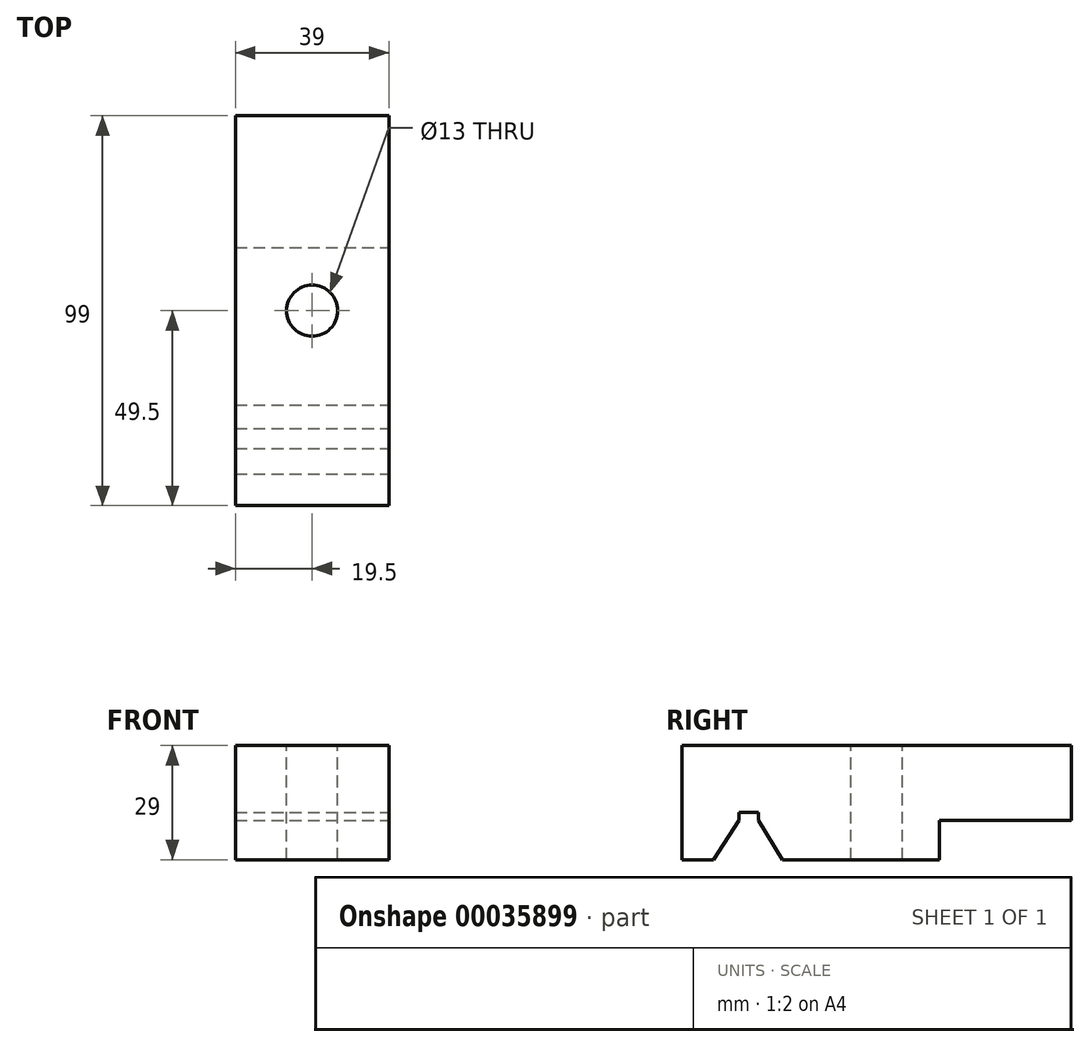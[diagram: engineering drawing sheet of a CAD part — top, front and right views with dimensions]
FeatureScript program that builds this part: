
annotation { "Feature Type Name" : "Feature", "Feature Type Description" : "" }
export const myFeature = defineFeature(function(context is Context, id is Id, definition is map)
    precondition{}
    {
        {
            var Q0;
            Q0=qCreatedBy(makeId("Right.planeOp"),FACE);
            var sketch = newSketch(context, id + "F0", { "sketchPlane" : qUnion([Q0])});
            skLineSegment(sketch, "E0", {"start": v(0, 0) * mm, "end": v(49.5, 0) * mm});
            skLineSegment(sketch, "E1", {"start": v(49.5, 0) * mm, "end": v(49.5, -19) * mm});
            skLineSegment(sketch, "E2", {"start": v(49.5, -19) * mm, "end": v(16, -19) * mm});
            skLineSegment(sketch, "E3", {"start": v(16, -19) * mm, "end": v(16, -29) * mm});
            skLineSegment(sketch, "E4", {"start": v(16, -29) * mm, "end": v(-24, -29) * mm});
            skLineSegment(sketch, "E5", {"start": v(-24, -29) * mm, "end": v(-30, -19) * mm});
            skLineSegment(sketch, "E6", {"start": v(-30, -19) * mm, "end": v(-30, -17) * mm});
            skLineSegment(sketch, "E7", {"start": v(-30, -17) * mm, "end": v(-35, -17) * mm});
            skLineSegment(sketch, "E8", {"start": v(-35, -17) * mm, "end": v(-35, -19) * mm});
            skLineSegment(sketch, "E9", {"start": v(-35, -19) * mm, "end": v(-41.5, -29) * mm});
            skLineSegment(sketch, "E10", {"start": v(-41.5, -29) * mm, "end": v(-49.5, -29) * mm});
            skLineSegment(sketch, "E11", {"start": v(-49.5, -29) * mm, "end": v(-49.5, 0) * mm});
            skLineSegment(sketch, "E12", {"start": v(-49.5, 0) * mm, "end": v(0, 0) * mm});
            skSolve(sketch);
        }
        {
            var Q0;
            Q0=makeQuery(id+"F0.imprint","IMPRINT",FACE,{"disambiguationData":[TD([[makeQuery(id+"F0.imprint","IMPRINT",EDGE,{"derivedFrom":sQuery(id+"F0.wireOp",EDGE,"E0")}),-1.0]])]});
            extrude(context, id + "F1", {"entities" : qUnion([Q0]), "oppositeDirection" : true, "depth" : 39 * mm});
        }
        {
            var Q0;
            Q0=qCreatedBy(makeId("Top.planeOp"),FACE);
            var sketch = newSketch(context, id + "F2", { "sketchPlane" : qUnion([Q0])});
            skLineSegment(sketch, "E13", {"start": v(0, 0) * mm, "end": v(-19.5, 0) * mm});
            skCircle(sketch, "E14", {"center": v(-19.5, 0) * mm, "radius": 6.5 * mm});
            skLineSegment(sketch, "E15", {"start": v(0, 0) * mm, "end": v(0, -52) * mm});
            skSolve(sketch);
        }
        {
            var Q0;
            Q0=makeQuery(id+"F2.imprint","IMPRINT",FACE,{"disambiguationData":[TD([[makeQuery(id+"F2.imprint","IMPRINT",EDGE,{"derivedFrom":sQuery(id+"F2.wireOp",EDGE,"E14")}),1.0]])]});
            extrude(context, id + "F3", {"entities" : qUnion([Q0]), "operationType" : NewBodyOperationType.REMOVE, "oppositeDirection" : true, "depth" : 35 * mm});
        }
    });
